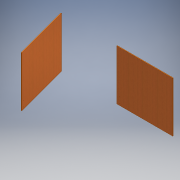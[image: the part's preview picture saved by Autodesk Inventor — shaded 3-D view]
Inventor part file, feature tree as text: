
AUTODESK INVENTOR PART (.ipt)
format: ipt  version: 2016 (Build 200138000, 138)  size: 175,616 bytes
history: native  units: mm
features: extrude x4, sketch x4, projected_geometry x2, plane x1
ambient origin geometry x8: Origin, YZ Plane, XZ Plane, XY Plane, X Axis, Y Axis, Z Axis, Center Point
bodies: Solid1 (feature_tree)
feature tree (11):
  plane  "Plano de trabajo4"
  extrude  "Extrusión8"  Depth=848.75mm
  extrude  "Extrusión9"  TaperAngle=0.0deg  [1 undecoded]
  extrude  "Extrusión10"  Depth=80.0mm
  extrude  "Extrusión11"  Depth=730.0mm
  sketch  "Boceto8"  dims[d38=290.0mm d39=848.75mm]
  sketch  "Boceto9"  dims[d40=10.0mm d42=0.0mm]
  projected_geometry  "Contorno proyectado7"
  sketch  "Boceto10"  dims[d43=42.4375mm d44=80.0mm]
  sketch  "Boceto11"  dims[d45=6.0mm d46=50.0mm d47=740.0mm d48=0.0mm d49=848.75mm d50=848.75mm d52=10.0mm d53=848.75mm d54=730.0mm d55=0.0mm d56=42.4375mm d57=80.0mm d58=6.0mm d59=50.0mm d60=730.0mm d61=0.0mm]
  projected_geometry  "Contorno proyectado8"
note: 1 required parameter value undecoded (feature->parameter linkage not recoverable at this tier; creation-order binding heuristic only, values carry confidence <= 0.55)
